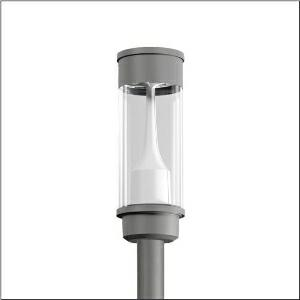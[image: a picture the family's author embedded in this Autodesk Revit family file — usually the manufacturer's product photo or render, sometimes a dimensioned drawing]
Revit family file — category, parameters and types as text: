
# Revit family: litepole_iq___st1_2a_5xa5415ef14h_6754
name_source: partatom
category: Lighting Fixtures
units: mm (PartAtom-declared; Revit-internal decimal feet)

## family parameters
Cut with Voids When Loaded = No
Host = Face
Light Source = No
Part Type = Normal
Room Calculation Point = No
Round Connector Dimension = Use Diameter
Shared = No

## types (1)
- --- (1 x LED, 1540 lm, 10.5 W, 3000K)
    Apparent Load = 11 VA
    CIE Flux Codes = 22 61 93 96 100
    Color Rendering = 70
    Color Temperature = 3000K
    Default Elevation = 1800 mm
    Description = Litepole iQ, mast luminaire, Module 540 iQ-SR, primary light control with 3 zone facetted reflector, of plastic, silver coated, highly specular, structured, primary optical cover: cover, of PMMA, transparent, light distribution: ST1.2a, light emission: direct distribution, primary light characteristic: asymmetric, installation type: post-top, LED, High Power LED, rated luminous flux: 1.540lm, luminous efficacy: 147lm/W, light colour: 730, colour temperature: 3000K, control gear: iQ Street-Remote, control: Auto-Match, Temp-Guard, Lumen-Switch, Night-Set, Smart-Wire, Light-Fading, Desk-Remote (wireless, voltage-free reading and setting of iQ features in the workshop via application-optimized NFC function/RFID function), optimised constant luminous flux control (CLO 2.0), Street-Remote, pre-setting: logarithmic dimming characteristic, with terminal, 6-pole, max. 2.5mm², mains connection: 230..240V, AC, 50/60Hz, start of lifetime: 11W, end of service life: 11W, reduction: 5W, luminaire housing, upper part, of glass-fibre reinforced polyester, coated, Siteco® metallic grey (DB 702S), diameter: 210mm, height: 590mm, spigot size: d x l = 76 x 70mm (post-top) | with reducer (optional accessory) 60 x 70mm, mounting height: 3..5m, post-top mast mounting element, of diecast aluminium, coated, Siteco® metallic grey (DB 702S), Module 540 iQ-SR, traffic white (RAL 9016), equipment: standard, protection rating (complete): IP65, insulation class (complete): insulation class II (safety insulation), certification: CE, ENEC, VDE, packaging unit: 1 piece

Light Distribution: ST1.2a
    Height = 590 mm
    Lamp = 1 x LED
    Lamp Light Flux = 1540 lm
    Lamp Power = 10.5 W
    Lamp count = 1
    Length = 220 mm
    Luminous efficacy = 147 lm/W
    Manufacturer = Siteco
    ModVariant = No
    Model = 5XA5415EF14H
    Number of Poles = 1
    OnlyDefault = Yes
    Power Factor = 1
    Product Name = Litepole iQ | ST1.2a
    Product group = mast luminaire | pylon top
    ProductGroupID = 6100
    Protection Class = Protection class II
    Protection Degree = IP 65
    RLX_Detail_Level = 1
    RLX_Emergency_Light_Flux = 0 lm
    RLX_Emergency_Type = 0
    RLX_Emergency_Type_DB = No
    RlxData = <blob elided: 71785 chars, md5=3aa855ff>
    Socket = socket
    Standby Power = 0 W
    System Light Flux = 1540 lm
    System Power = 11 W
    Type Comments = factory setting: luminous flux: 100 % | dim-lin: 254 | 419 mA
    Type Image = l_1006025.jpg
    URL = http://relux.com
    VarID = @adj_180325
    Voltage = 0 V
    Weight = 0.00 kg
    Width = 0 mm  [stored 0 ft]

note: [stored X ft] marks values corroborated as IEEE doubles in the binary element streams (Revit-internal decimal feet)

## geometry (parser evidence)
native form markers: Blend x4, Sweep x11
no freeform markers — native parametric forms only
